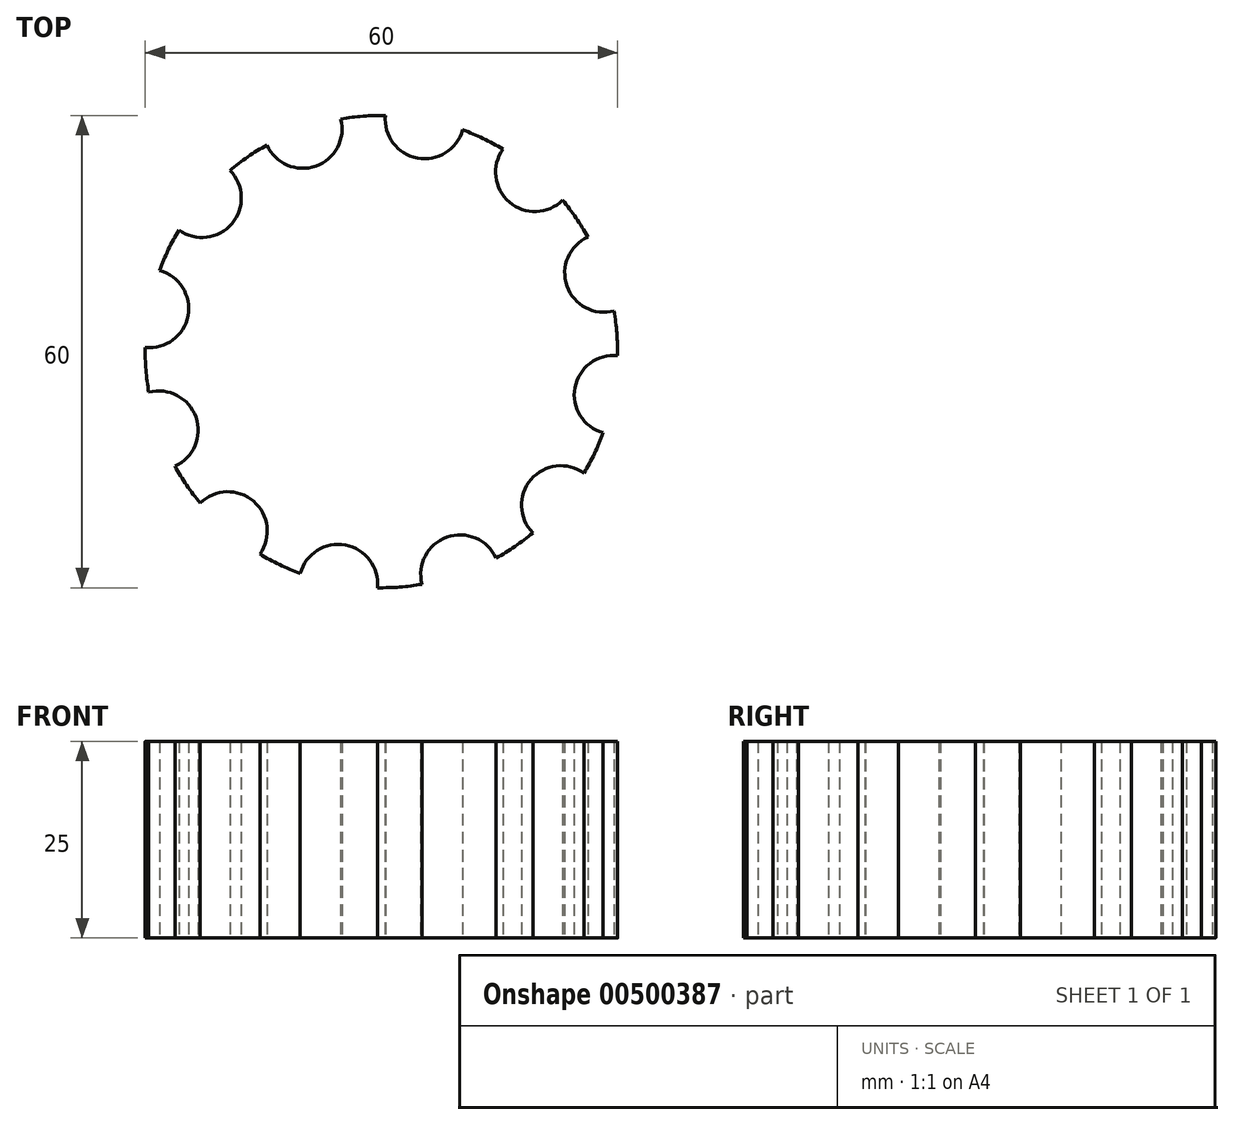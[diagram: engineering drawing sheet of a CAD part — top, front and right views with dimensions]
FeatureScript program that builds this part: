
annotation { "Feature Type Name" : "Feature", "Feature Type Description" : "" }
export const myFeature = defineFeature(function(context is Context, id is Id, definition is map)
    precondition{}
    {
        {
            var Q0;
            Q0=qCreatedBy(makeId("Top.planeOp"),FACE);
            var sketch = newSketch(context, id + "F0", { "sketchPlane" : qUnion([Q0])});
            skCircle(sketch, "E0", {"center": v(0, 0) * mm, "radius": 30 * mm});
            skArc(sketch, "E1", {"start": v(0.51, 30) * mm, "mid": v(4.57, 24.58) * mm, "end": v(10.3, 28.17) * mm});
            skArc(sketch, "E2.1.0", {"start": v(-14.55, 26.23) * mm, "mid": v(-8.33, 23.57) * mm, "end": v(-5.16, 29.55) * mm});
            skCircle(sketch, "E2.2.0", {"center": v(-22.8, 19.5) * mm, "radius": 5 * mm});
            skCircle(sketch, "E2.3.0", {"center": v(-29.5, 5.49) * mm, "radius": 5 * mm});
            skCircle(sketch, "E2.4.0", {"center": v(-28.29, -10) * mm, "radius": 5 * mm});
            skCircle(sketch, "E2.5.0", {"center": v(-19.5, -22.8) * mm, "radius": 5 * mm});
            skCircle(sketch, "E2.6.0", {"center": v(-5.49, -29.5) * mm, "radius": 5 * mm});
            skCircle(sketch, "E2.7.0", {"center": v(10, -28.29) * mm, "radius": 5 * mm});
            skCircle(sketch, "E2.8.0", {"center": v(22.8, -19.5) * mm, "radius": 5 * mm});
            skArc(sketch, "E2.8.1", {"start": v(0.51, 30) * mm, "mid": v(-5.49, -29.5) * mm, "end": v(10.3, 28.17) * mm});
            skCircle(sketch, "E2.9.0", {"center": v(29.5, -5.49) * mm, "radius": 5 * mm});
            skArc(sketch, "E2.10.0", {"start": v(26.23, 14.55) * mm, "mid": v(23.57, 8.33) * mm, "end": v(29.55, 5.16) * mm});
            skArc(sketch, "E2.10.1", {"start": v(5.49, 29.5) * mm, "mid": v(-7.93, -28.93) * mm, "end": v(10.3, 28.17) * mm});
            skArc(sketch, "E2.11.0", {"start": v(15.44, 25.72) * mm, "mid": v(16.25, 19) * mm, "end": v(23.01, 19.24) * mm});
            skSolve(sketch);
        }
        {
            var Q0;
            {var subQ5=sQuery(id+"F0.wireOp",EDGE,"E1");Q0=makeQuery(id+"F0.imprint","IMPRINT",FACE,{"disambiguationData":[TD([[makeQuery(id+"F0.imprint","IMPRINT",EDGE,{"derivedFrom":subQ5}),-1.0]])]});}
            extrude(context, id + "F1", {"entities" : qUnion([Q0]), "depth" : 25 * mm});
        }
    });
